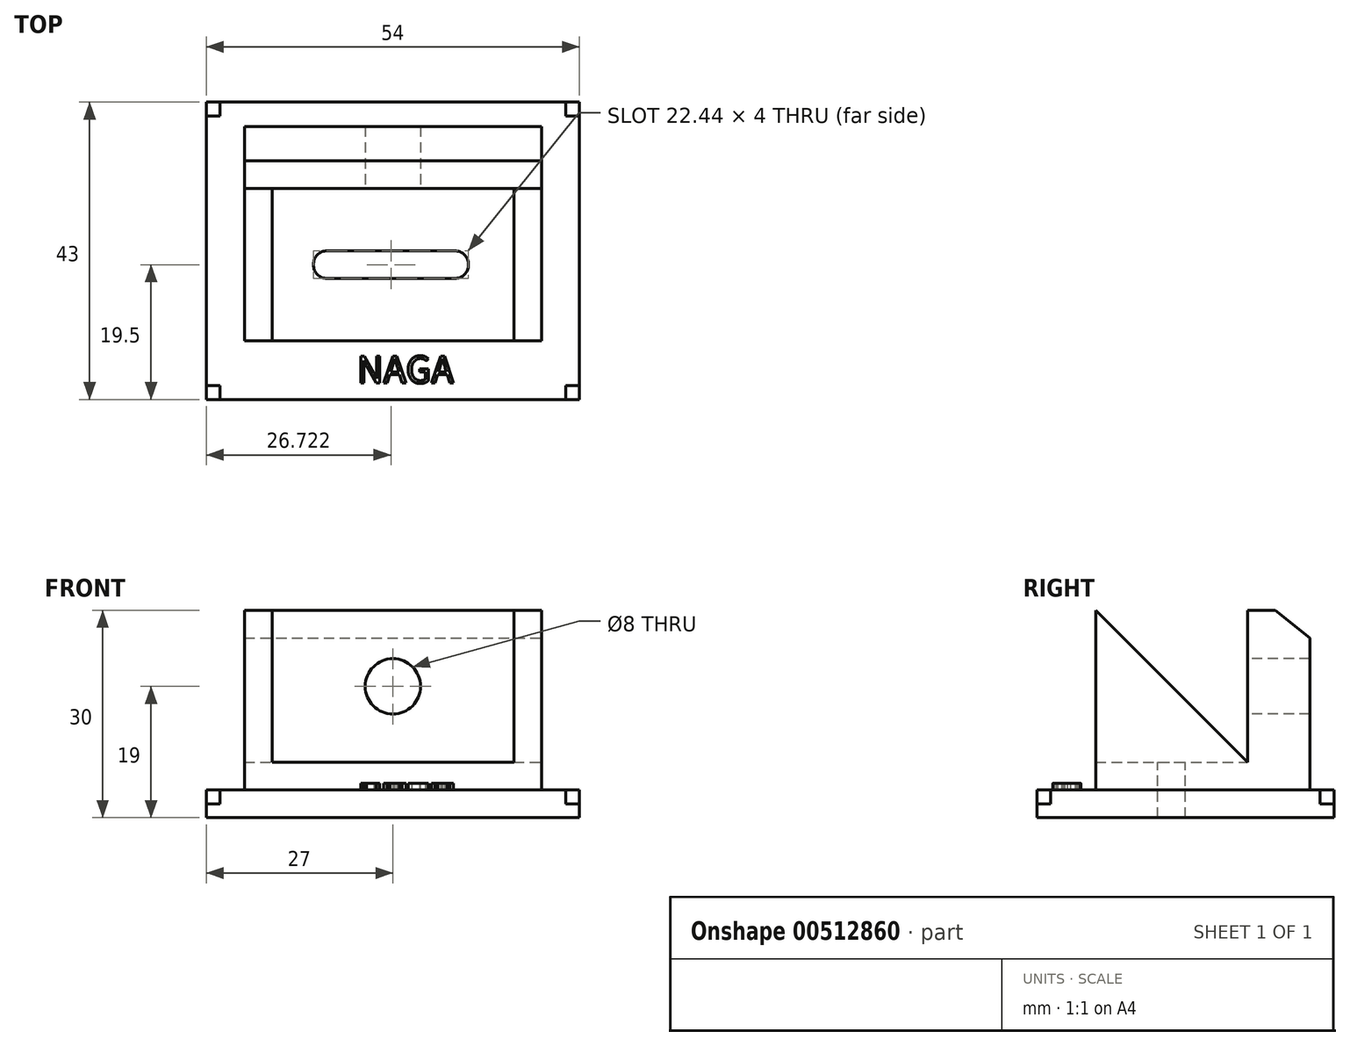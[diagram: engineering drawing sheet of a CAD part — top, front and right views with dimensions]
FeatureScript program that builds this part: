
annotation { "Feature Type Name" : "Feature", "Feature Type Description" : "" }
export const myFeature = defineFeature(function(context is Context, id is Id, definition is map)
    precondition{}
    {
        {
            var Q0;
            Q0=qCreatedBy(makeId("Top.planeOp"),FACE);
            var sketch = newSketch(context, id + "F0", { "sketchPlane" : qUnion([Q0])});
            skLineSegment(sketch, "E0.bottom", {"start": v(21.5, -13) * mm, "end": v(-21.5, -13) * mm});
            skLineSegment(sketch, "E0.top", {"start": v(21.5, 13) * mm, "end": v(-21.5, 13) * mm});
            skLineSegment(sketch, "E0.left", {"start": v(21.5, -13) * mm, "end": v(21.5, 13) * mm});
            skLineSegment(sketch, "E0.right", {"start": v(-21.5, -13) * mm, "end": v(-21.5, 13) * mm});
            skPoint(sketch, "E0.middle", {"position": v(0, 0) * mm});
            skLineSegment(sketch, "E1.bottom", {"start": v(27, -21.5) * mm, "end": v(-27, -21.5) * mm});
            skLineSegment(sketch, "E1.top", {"start": v(27, 21.5) * mm, "end": v(-27, 21.5) * mm});
            skLineSegment(sketch, "E1.left", {"start": v(27, -21.5) * mm, "end": v(27, 21.5) * mm});
            skLineSegment(sketch, "E1.right", {"start": v(-27, -21.5) * mm, "end": v(-27, 21.5) * mm});
            skSolve(sketch);
        }
        {
            var Q0;
            Q0=makeQuery(id+"F0.imprint","IMPRINT",FACE,{"disambiguationData":[TD([[makeQuery(id+"F0.imprint","IMPRINT",EDGE,{"derivedFrom":sQuery(id+"F0.wireOp",EDGE,"E0.bottom")}),-1.0]])]});
            extrude(context, id + "F1", {"entities" : qUnion([Q0]), "depth" : 26 * mm});
        }
        {
            var Q0;
            Q0=makeQuery(id+"F1.opExtrude","CAP_FACE",FACE,{"disambiguationData":[OSD([sQuery(id+"F0.wireOp",EDGE,"E0.bottom"),sQuery(id+"F0.wireOp",EDGE,"E0.top"),sQuery(id+"F0.wireOp",EDGE,"E0.left"),sQuery(id+"F0.wireOp",EDGE,"E0.right")])],"isStart":false});
            var sketch = newSketch(context, id + "F2", { "sketchPlane" : qUnion([Q0])});
            skLineSegment(sketch, "E2.bottom", {"start": v(-17.5, -13) * mm, "end": v(17.5, -13) * mm});
            skLineSegment(sketch, "E2.top", {"start": v(-17.5, 9) * mm, "end": v(17.5, 9) * mm});
            skLineSegment(sketch, "E2.left", {"start": v(-17.5, -13) * mm, "end": v(-17.5, 9) * mm});
            skLineSegment(sketch, "E2.right", {"start": v(17.5, -13) * mm, "end": v(17.5, 9) * mm});
            skSolve(sketch);
        }
        {
            var Q0;
            Q0 = qSketchRegion(id + "F2", true);
            extrude(context, id + "F3", {"entities" : qUnion([Q0]), "operationType" : NewBodyOperationType.REMOVE, "oppositeDirection" : true, "depth" : 22 * mm});
        }
        {
            var Q0;
            Q0=makeQuery(id+"F0.imprint","IMPRINT",FACE,{"disambiguationData":[TD([[makeQuery(id+"F0.imprint","IMPRINT",EDGE,{"derivedFrom":sQuery(id+"F0.wireOp",EDGE,"E0.bottom")}),-1.0]])]});
            var Q1;
            Q1=makeQuery(id+"F0.imprint","IMPRINT",FACE,{"disambiguationData":[TD([[makeQuery(id+"F0.imprint","IMPRINT",EDGE,{"derivedFrom":sQuery(id+"F0.wireOp",EDGE,"E0.bottom")}),1.0]])]});
            extrude(context, id + "F4", {"entities" : qUnion([Q0, Q1]), "operationType" : NewBodyOperationType.ADD, "oppositeDirection" : true, "depth" : 4 * mm});
        }
        {
            var Q0;
            Q0=makeQuery(id+"F4.opExtrude","SWEPT_FACE",FACE,{"disambiguationData":[OSD([sQuery(id+"F0.wireOp",EDGE,"E1.bottom")])]});
            var sketch = newSketch(context, id + "F5", { "sketchPlane" : qUnion([Q0])});
            skLineSegment(sketch, "E3.bottom", {"start": v(-27, 0) * mm, "end": v(-25, 0) * mm});
            skLineSegment(sketch, "E3.top", {"start": v(-27, -2) * mm, "end": v(-25, -2) * mm});
            skLineSegment(sketch, "E3.left", {"start": v(-27, 0) * mm, "end": v(-27, -2) * mm});
            skLineSegment(sketch, "E3.right", {"start": v(-25, 0) * mm, "end": v(-25, -2) * mm});
            skLineSegment(sketch, "E4.bottom", {"start": v(27, 0) * mm, "end": v(25, 0) * mm});
            skLineSegment(sketch, "E4.top", {"start": v(27, -2) * mm, "end": v(25, -2) * mm});
            skLineSegment(sketch, "E4.left", {"start": v(27, 0) * mm, "end": v(27, -2) * mm});
            skLineSegment(sketch, "E4.right", {"start": v(25, 0) * mm, "end": v(25, -2) * mm});
            skSolve(sketch);
        }
        {
            var Q0;
            Q0 = qSketchRegion(id + "F5", true);
            extrude(context, id + "F6", {"entities" : qUnion([Q0]), "operationType" : NewBodyOperationType.REMOVE, "oppositeDirection" : true, "depth" : 2 * mm});
        }
        {
            var Q0;
            Q0 = qSketchRegion(id + "F5", true);
            extrude(context, id + "F7", {"entities" : qUnion([Q0]), "operationType" : NewBodyOperationType.REMOVE, "oppositeDirection" : true, "depth" : 2 * mm});
        }
        {
            var Q0;
            Q0=makeQuery(id+"F4.opExtrude","SWEPT_FACE",FACE,{"disambiguationData":[OSD([sQuery(id+"F0.wireOp",EDGE,"E1.top")])]});
            var sketch = newSketch(context, id + "F8", { "sketchPlane" : qUnion([Q0])});
            skLineSegment(sketch, "E5.0", {"start": v(-25, 0) * mm, "end": v(-25, -2) * mm});
            skLineSegment(sketch, "E6.0", {"start": v(-27, -2) * mm, "end": v(-27, 0) * mm});
            skLineSegment(sketch, "E7.0", {"start": v(-27, -2) * mm, "end": v(-25, -2) * mm});
            skLineSegment(sketch, "E8.0", {"start": v(-27, 0) * mm, "end": v(-25, 0) * mm});
            skLineSegment(sketch, "E9.0.0", {"start": v(25, -2) * mm, "end": v(25, 0) * mm});
            skLineSegment(sketch, "E9.0.1", {"start": v(25, 0) * mm, "end": v(27, 0) * mm});
            skLineSegment(sketch, "E9.0.2", {"start": v(27, 0) * mm, "end": v(27, -2) * mm});
            skLineSegment(sketch, "E9.0.3", {"start": v(27, -2) * mm, "end": v(25, -2) * mm});
            skSolve(sketch);
        }
        {
            var Q0;
            Q0 = qSketchRegion(id + "F8", true);
            extrude(context, id + "F9", {"entities" : qUnion([Q0]), "operationType" : NewBodyOperationType.REMOVE, "oppositeDirection" : true, "depth" : 2 * mm});
        }
        {
            var Q0;
            Q0=makeQuery(id+"F3.boolean.opBoolean","COPY",FACE,{"derivedFrom":makeQuery(id+"F3.opExtrude","CAP_FACE",FACE,{"disambiguationData":[OSD([sQuery(id+"F2.wireOp",EDGE,"E2.bottom"),sQuery(id+"F2.wireOp",EDGE,"E2.top"),sQuery(id+"F2.wireOp",EDGE,"E2.left"),sQuery(id+"F2.wireOp",EDGE,"E2.right")])],"isStart":false})});
            var sketch = newSketch(context, id + "F10", { "sketchPlane" : qUnion([Q0])});
            skLineSegment(sketch, "E10", {"start": v(-9.5, 0) * mm, "end": v(8.94, 0) * mm});
            skLineSegment(sketch, "E11", {"start": v(8.94, 0) * mm, "end": v(8.94, -4) * mm});
            skLineSegment(sketch, "E12", {"start": v(8.94, -4) * mm, "end": v(-9.5, -4) * mm});
            skLineSegment(sketch, "E13", {"start": v(-9.5, -4) * mm, "end": v(-9.5, 0) * mm});
            skArc(sketch, "E14", {"start": v(-9.5, 0) * mm, "mid": v(-11.5, -2) * mm, "end": v(-9.5, -4) * mm});
            skLineSegment(sketch, "E15", {"start": v(0, 1.02) * mm, "end": v(0, 1.02) * mm});
            skLineSegment(sketch, "E16", {"start": v(-0.28, -6.71) * mm, "end": v(-0.28, 5.18) * mm, "construction": true});
            skPoint(sketch, "E16.startSnap0", {"position": v(-0.28, -4) * mm});
            skArc(sketch, "E17.MirrorCS", {"start": v(8.94, 0) * mm, "mid": v(10.94, -2) * mm, "end": v(8.94, -4) * mm});
            skSolve(sketch);
        }
        {
            var Q0;
            Q0 = qSketchRegion(id + "F10", true);
            extrude(context, id + "F11", {"entities" : qUnion([Q0]), "operationType" : NewBodyOperationType.REMOVE, "oppositeDirection" : true, "depth" : 25 * mm});
        }
        {
            var Q0;
            Q0=makeQuery(id+"F3.boolean.opBoolean","COPY",FACE,{"derivedFrom":makeQuery(id+"F3.opExtrude","SWEPT_FACE",FACE,{"disambiguationData":[OSD([sQuery(id+"F2.wireOp",EDGE,"E2.left")])]})});
            var sketch = newSketch(context, id + "F12", { "sketchPlane" : qUnion([Q0])});
            skLineSegment(sketch, "E18.0", {"start": v(-13, 4) * mm, "end": v(9, 4) * mm});
            skLineSegment(sketch, "E19.0", {"start": v(-13, 4) * mm, "end": v(-13, 26) * mm});
            skLineSegment(sketch, "E20.0", {"start": v(-13, 26) * mm, "end": v(9, 26) * mm});
            skLineSegment(sketch, "E21.0", {"start": v(9, 4) * mm, "end": v(9, 26) * mm});
            skLineSegment(sketch, "E22", {"start": v(-13, 4) * mm, "end": v(9, 26) * mm});
            skLineSegment(sketch, "E23", {"start": v(-13, 26) * mm, "end": v(9, 4) * mm});
            skCircle(sketch, "E24", {"center": v(-2, 15) * mm, "radius": 4 * mm});
            skSolve(sketch);
        }
        {
            var Q0;
            {var subQ0=sQuery(id+"F12.wireOp",EDGE,"E24");var subQ1=sQuery(id+"F12.wireOp",EDGE,"E22");var subQ2=makeQuery(id+"F12.imprint","INTERSECT",VERTEX,{"disambiguationData":[OD(0.0)],"derivedFrom":[subQ1,subQ0]});Q0=makeQuery(id+"F12.imprint","IMPRINT",FACE,{"disambiguationData":[TD([[makeQuery(id+"F12.imprint","IMPRINT",EDGE,{"disambiguationData":[TD([[subQ2,-1.0]])],"derivedFrom":subQ1}),-1.0]])]});}
            var Q1;
            {var subQ0=sQuery(id+"F12.wireOp",EDGE,"E24");var subQ1=sQuery(id+"F12.wireOp",EDGE,"E22");var subQ2=makeQuery(id+"F12.imprint","INTERSECT",VERTEX,{"disambiguationData":[OD(0.0)],"derivedFrom":[subQ1,subQ0]});Q1=makeQuery(id+"F12.imprint","IMPRINT",FACE,{"disambiguationData":[TD([[makeQuery(id+"F12.imprint","IMPRINT",EDGE,{"disambiguationData":[TD([[subQ2,-1.0]])],"derivedFrom":subQ1}),1.0]])]});}
            var Q2;
            {var subQ0=sQuery(id+"F12.wireOp",EDGE,"E23");var subQ1=sQuery(id+"F12.wireOp",EDGE,"E22");var subQ2=makeQuery(id+"F12.imprint","INTERSECT",VERTEX,{"derivedFrom":[subQ1,subQ0]});Q2=makeQuery(id+"F12.imprint","IMPRINT",FACE,{"disambiguationData":[TD([[makeQuery(id+"F12.imprint","IMPRINT",EDGE,{"disambiguationData":[TD([[subQ2,-1.0]])],"derivedFrom":subQ1}),-1.0]])]});}
            var Q3;
            {var subQ0=sQuery(id+"F12.wireOp",EDGE,"E23");var subQ1=sQuery(id+"F12.wireOp",EDGE,"E22");var subQ2=makeQuery(id+"F12.imprint","INTERSECT",VERTEX,{"derivedFrom":[subQ1,subQ0]});Q3=makeQuery(id+"F12.imprint","IMPRINT",FACE,{"disambiguationData":[TD([[makeQuery(id+"F12.imprint","IMPRINT",EDGE,{"disambiguationData":[TD([[subQ2,-1.0]])],"derivedFrom":subQ1}),1.0]])]});}
            extrude(context, id + "F13", {"entities" : qUnion([Q0, Q1, Q2, Q3]), "operationType" : NewBodyOperationType.REMOVE, "oppositeDirection" : true, "depth" : 50 * mm, "hasSecondDirection" : true, "secondDirectionOppositeDirection" : false, "secondDirectionDepth" : 50 * mm});
        }
        {
            var Q0;
            Q0=makeQuery(id+"F1.opExtrude","SWEPT_FACE",FACE,{"disambiguationData":[OSD([sQuery(id+"F0.wireOp",EDGE,"E0.left")])]});
            var sketch = newSketch(context, id + "F14", { "sketchPlane" : qUnion([Q0])});
            skLineSegment(sketch, "E25.bottom", {"start": v(13, 0) * mm, "end": v(18, 0) * mm});
            skLineSegment(sketch, "E25.top", {"start": v(13, 26) * mm, "end": v(18, 26) * mm});
            skLineSegment(sketch, "E25.left", {"start": v(13, 0) * mm, "end": v(13, 26) * mm});
            skLineSegment(sketch, "E25.right", {"start": v(18, 0) * mm, "end": v(18, 26) * mm});
            skSolve(sketch);
        }
        {
            var Q0;
            Q0=makeQuery(id+"F14.imprint","IMPRINT",FACE,{"disambiguationData":[TD([[makeQuery(id+"F14.imprint","IMPRINT",EDGE,{"derivedFrom":sQuery(id+"F14.wireOp",EDGE,"E25.bottom")}),1.0]])]});
            extrude(context, id + "F15", {"entities" : qUnion([Q0]), "operationType" : NewBodyOperationType.ADD, "oppositeDirection" : true, "depth" : 43 * mm});
        }
        {
            var Q0;
            Q0=makeQuery(id+"F15.boolean.opBoolean","MERGE",FACE,{"derivedFrom":[makeQuery(id+"F1.opExtrude","SWEPT_FACE",FACE,{"disambiguationData":[OSD([sQuery(id+"F0.wireOp",EDGE,"E0.left")])]}),makeQuery(id+"F15.opExtrude","CAP_FACE",FACE,{"disambiguationData":[OSD([sQuery(id+"F14.wireOp",EDGE,"E25.bottom"),sQuery(id+"F14.wireOp",EDGE,"E25.top"),sQuery(id+"F14.wireOp",EDGE,"E25.left"),sQuery(id+"F14.wireOp",EDGE,"E25.right")])],"isStart":true})]});
            var sketch = newSketch(context, id + "F16", { "sketchPlane" : qUnion([Q0])});
            skLineSegment(sketch, "E26", {"start": v(18, 26) * mm, "end": v(18, 22) * mm});
            skLineSegment(sketch, "E27", {"start": v(18, 22) * mm, "end": v(13, 26) * mm});
            skLineSegment(sketch, "E28", {"start": v(13, 26) * mm, "end": v(18, 26) * mm});
            skSolve(sketch);
        }
        {
            var Q0;
            Q0 = qSketchRegion(id + "F16", true);
            extrude(context, id + "F17", {"entities" : qUnion([Q0]), "operationType" : NewBodyOperationType.REMOVE, "oppositeDirection" : true, "depth" : 46 * mm});
        }
        {
            var Q0;
            Q0=makeQuery(id+"F3.boolean.opBoolean","COPY",FACE,{"derivedFrom":makeQuery(id+"F3.opExtrude","SWEPT_FACE",FACE,{"disambiguationData":[OSD([sQuery(id+"F2.wireOp",EDGE,"E2.top")])]})});
            var sketch = newSketch(context, id + "F18", { "sketchPlane" : qUnion([Q0])});
            skLineSegment(sketch, "E29", {"start": v(-17.5, 26) * mm, "end": v(17.5, 4) * mm});
            skLineSegment(sketch, "E30", {"start": v(17.5, 26) * mm, "end": v(-17.5, 4) * mm});
            skCircle(sketch, "E31", {"center": v(0, 15) * mm, "radius": 4 * mm});
            skSolve(sketch);
        }
        {
            var Q0;
            Q0 = qSketchRegion(id + "F18", true);
            extrude(context, id + "F19", {"entities" : qUnion([Q0]), "operationType" : NewBodyOperationType.REMOVE, "oppositeDirection" : true, "depth" : 25 * mm});
        }
        {
            var Q0;
            Q0=makeQuery(id+"F4.opExtrude","CAP_FACE",FACE,{"disambiguationData":[OSD([sQuery(id+"F0.wireOp",EDGE,"E1.bottom"),sQuery(id+"F0.wireOp",EDGE,"E1.top"),sQuery(id+"F0.wireOp",EDGE,"E1.left"),sQuery(id+"F0.wireOp",EDGE,"E1.right")])],"isStart":true});
            var sketch = newSketch(context, id + "F20", { "sketchPlane" : qUnion([Q0])});
            skText(sketch, "E32", { "text": "NAGA", "fontName": "NotoSansCJKjp-Regular.otf"});
            const initialGuessF20  = {"E32": [-0.0052, -0.01913, 1, 0, 0.00384]};
            skSetInitialGuess(sketch, initialGuessF20);
            skSolve(sketch);
        }
        {
            var Q0;
            Q0 = qSketchRegion(id + "F20", true);
            extrude(context, id + "F21", {"entities" : qUnion([Q0]), "operationType" : NewBodyOperationType.ADD, "depth" : 1 * mm, "offsetDistance" : 25 * mm});
        }
    });
